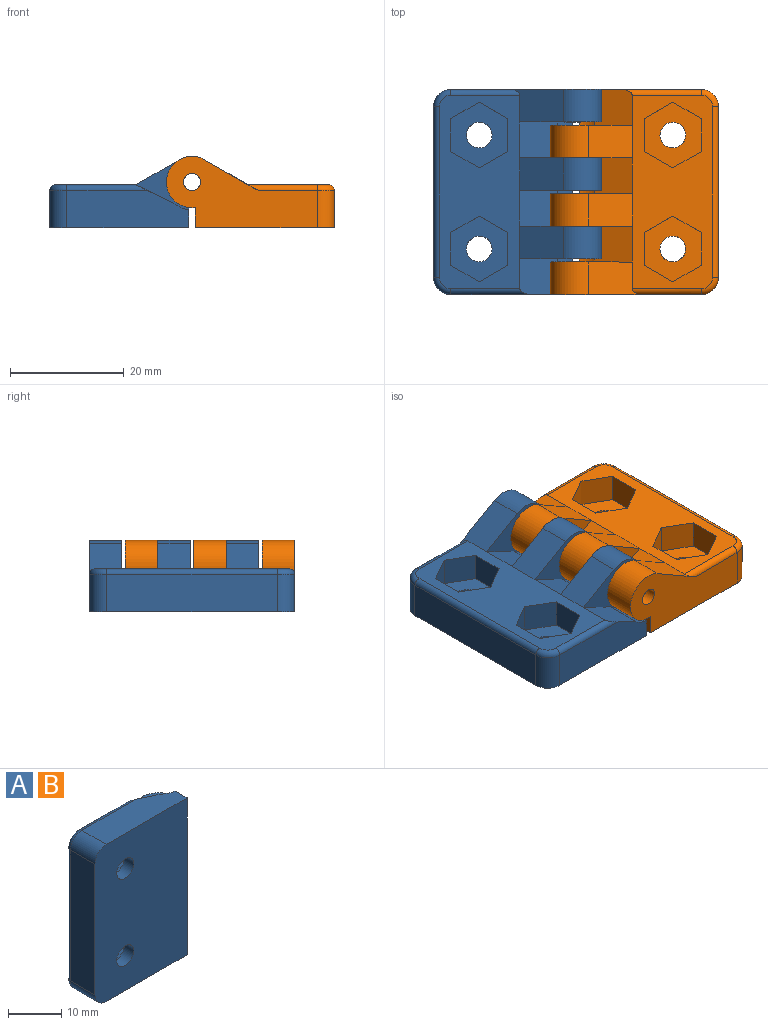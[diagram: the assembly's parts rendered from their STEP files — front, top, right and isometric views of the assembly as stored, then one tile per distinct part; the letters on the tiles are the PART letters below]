
ASSEMBLY  parts=2 mates=2
PART A: 52 faces, bbox 29.7x12.5x36.5 mm
  f0: plane 34x14.13mm, normal (0,1,0), area 305.6mm2, adj f3,f8,f12,f22,f26,f30,f33,f34
  f1: cylinder r=2.25mm len=4.5mm, axis (0,1,0), area 35.3mm2, adj f17,f45
  f2: cylinder r=2.25mm len=4.5mm, axis (0,1,0), area 35.3mm2, adj f17,f38
  f3: plane 9.35x5.7mm, normal (-0.5,0.87,0), area 50.6mm2, adj f0,f4,f18,f27,f37
  f4: cylinder r=4.5mm len=9mm, axis (0,0,1), area 94mm2, adj f3,f5,f18,f27
  f5: plane 5.7x0.6mm, normal (0,-1,0), area 3.4mm2, adj f4,f7,f18,f27
  f6: cylinder r=1.5mm len=5.7mm, axis (0,0,1), area 53.7mm2, adj f18,f27
  f7: plane 36x3.5mm, normal (1,0,0), area 119.5mm2, adj f5,f10,f14,f17,f18,f19,f20,f21
  f8: plane 7.62x5.7mm, normal (-0.5,0.87,0), area 50.1mm2, adj f0,f9,f23,f28
  f9: cylinder r=4.5mm len=9mm, axis (0,0,1), area 94mm2, adj f8,f10,f23,f28
  f10: plane 5.7x0.6mm, normal (0,-1,0), area 3.4mm2, adj f7,f9,f23,f28
  f11: cylinder r=1.5mm len=5.7mm, axis (0,0,1), area 53.7mm2, adj f23,f28
  f12: plane 7.62x5.7mm, normal (-0.5,0.87,0), area 50.1mm2, adj f0,f13,f20,f24
  f13: cylinder r=4.5mm len=9mm, axis (0,0,1), area 94mm2, adj f12,f14,f20,f24
  f14: plane 5.7x0.6mm, normal (0,-1,0), area 3.4mm2, adj f7,f13,f20,f24
  f15: cylinder r=1.5mm len=5.7mm, axis (0,0,1), area 53.7mm2, adj f20,f24
  f16: plane 30x6.5mm, normal (-1,0,0), area 195mm2, adj f17,f31,f32,f35
  f17: plane 36x24.4mm, normal (0,-1,0), area 842.7mm2, adj f1,f2,f7,f16,f18,f19,f31,f32
  f18: plane 26.5x12.5mm, normal (0,0,-1), area 203.9mm2, adj f3,f4,f5,f6,f7,f17,f31,f37
  f19: plane 21.4x6.5mm, normal (0,0,1), area 126.5mm2, adj f7,f17,f21,f22,f32,f33
  f20: plane 14.37x9.34mm, normal (0,0,1), area 75.5mm2, adj f7,f12,f13,f14,f15,f21,f22
  f21: cylinder r=4.88mm len=6.3mm, axis (0,0,1), area 18.1mm2, adj f7,f19,f20,f22
  f22: plane 6.67x6.3mm, normal (0.43,0.9,0), area 46.1mm2, adj f0,f19,f20,f21,f33
  f23: plane 14.37x9.34mm, normal (0,0,1), area 75.5mm2, adj f7,f8,f9,f10,f11,f25,f26
  f24: plane 14.37x9.34mm, normal (0,0,-1), area 75.5mm2, adj f7,f12,f13,f14,f15,f25,f26
  f25: cylinder r=4.88mm len=6.3mm, axis (0,0,1), area 18.1mm2, adj f7,f23,f24,f26
  f26: plane 6.67x6.3mm, normal (0.43,0.9,0), area 46.6mm2, adj f0,f23,f24,f25
  f27: plane 14.37x9.34mm, normal (0,0,1), area 75.5mm2, adj f3,f4,f5,f6,f7,f29,f30
  f28: plane 14.37x9.34mm, normal (0,0,-1), area 75.5mm2, adj f7,f8,f9,f10,f11,f29,f30
  f29: cylinder r=4.88mm len=6.3mm, axis (0,0,1), area 18.1mm2, adj f7,f27,f28,f30
  f30: plane 6.67x6.3mm, normal (0.43,0.9,0), area 46.6mm2, adj f0,f27,f28,f29
  f31: cylinder r=3mm len=6.5mm, axis (0,1,0), area 30.6mm2, adj f16,f17,f18,f36
  f32: cylinder r=3mm len=6.5mm, axis (0,-1,0), area 30.6mm2, adj f16,f17,f19,f34
  f33: cylinder r=1mm len=14.23mm, axis (-1,0,0), area 20.3mm2, adj f0,f19,f22,f34
  f34: torus R=2mm, axis (0,1,0), area 6.5mm2, adj f0,f32,f33,f35
  f35: cylinder r=1mm len=30mm, axis (0,0,1), area 47.1mm2, adj f0,f16,f34,f36
  f36: torus R=2mm, axis (0,1,0), area 6.5mm2, adj f0,f31,f35,f37
  f37: cylinder r=1mm len=12.13mm, axis (1,0,0), area 18.1mm2, adj f0,f3,f18,f36
  f38: plane 11.55x10mm, normal (0,1,0), area 70.7mm2, adj f2,f39,f40,f41,f42,f43,f44
  f39: plane 5.77x5mm, normal (1,0,0), area 28.9mm2, adj f0,f38,f40,f44
  f40: plane 5x5mm, normal (0.5,0,-0.87), area 28.9mm2, adj f0,f38,f39,f41
  f41: plane 5x5mm, normal (-0.5,0,-0.87), area 28.9mm2, adj f0,f38,f40,f42
  f42: plane 5.77x5mm, normal (-1,0,0), area 28.9mm2, adj f0,f38,f41,f43
  f43: plane 5x5mm, normal (-0.5,0,0.87), area 28.9mm2, adj f0,f38,f42,f44
  f44: plane 5x5mm, normal (0.5,0,0.87), area 28.9mm2, adj f0,f38,f39,f43
  f45: plane 11.55x10mm, normal (0,1,0), area 70.7mm2, adj f1,f46,f47,f48,f49,f50,f51
  f46: plane 5.77x5mm, normal (1,0,0), area 28.9mm2, adj f0,f45,f47,f51
  f47: plane 5x5mm, normal (0.5,0,-0.87), area 28.9mm2, adj f0,f45,f46,f48
  f48: plane 5x5mm, normal (-0.5,0,-0.87), area 28.9mm2, adj f0,f45,f47,f49
  f49: plane 5.77x5mm, normal (-1,0,0), area 28.9mm2, adj f0,f45,f48,f50
  f50: plane 5x5mm, normal (-0.5,0,0.87), area 28.9mm2, adj f0,f45,f49,f51
  f51: plane 5x5mm, normal (0.5,0,0.87), area 28.9mm2, adj f0,f45,f46,f50
PART B: same geometry as A
PLACE A rot(axis=(1,0,0),90deg) t=(-26.43,-18.29,-27.67)mm
PLACE B rot(axis=(0,-0.71,-0.71),180deg) t=(3.57,17.71,-27.67)mm
MATE planar B.f18 <-> A.f19  axis (0,-1,0) through (-3.28,-18.29,-26.81)mm
MATE cylindrical A.f4 <-> B.f4  axis (0,-1,0) through (-11.43,-11.99,-23.67)mm
